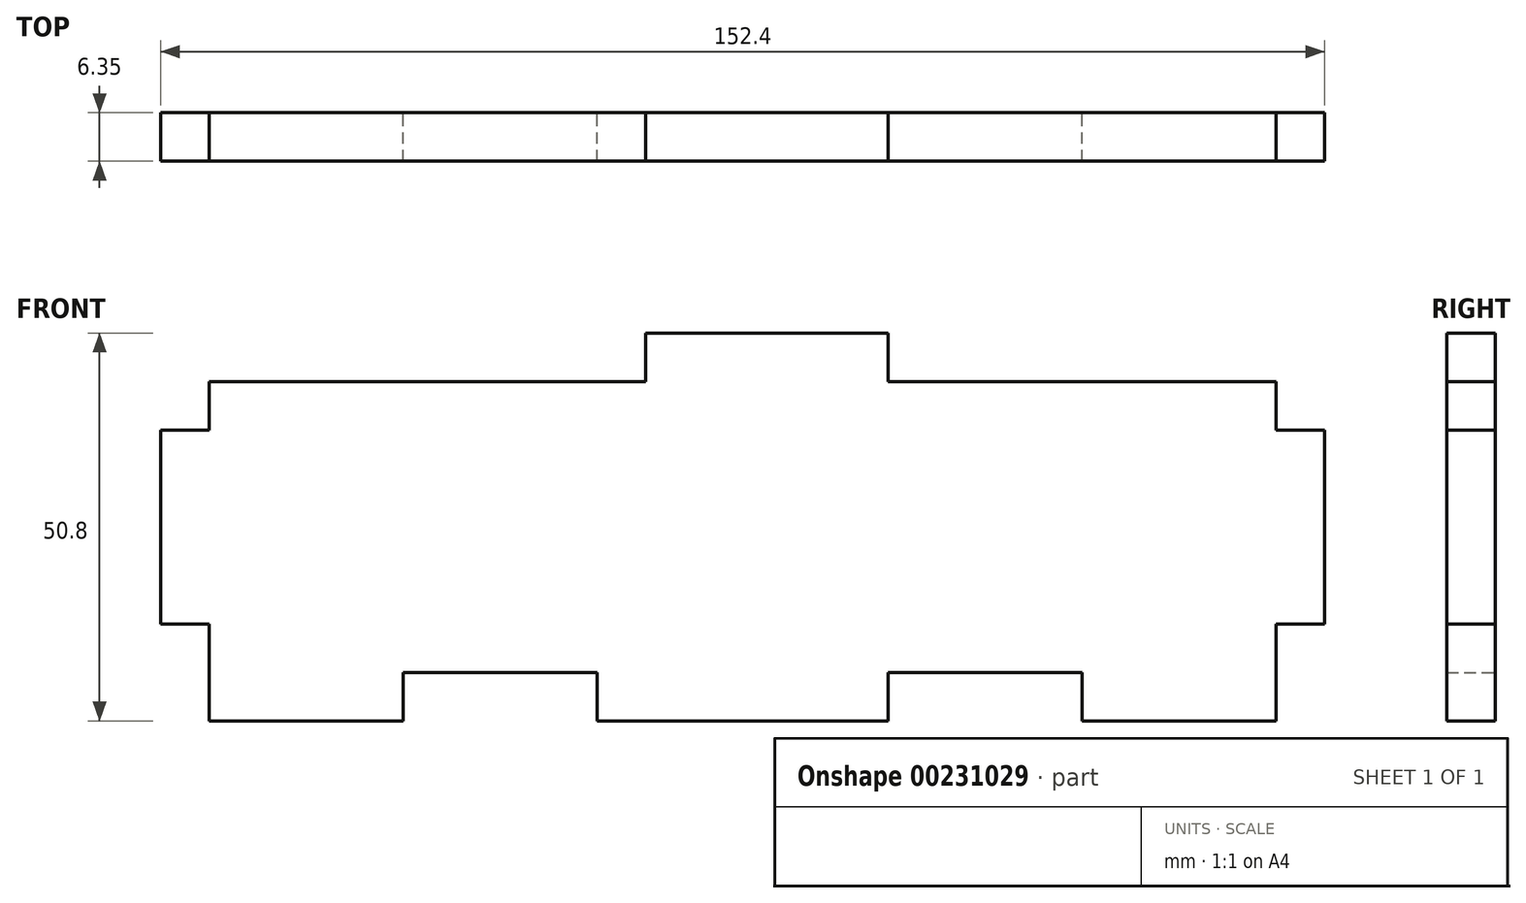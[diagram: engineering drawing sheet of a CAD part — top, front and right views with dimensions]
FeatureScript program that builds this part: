
annotation { "Feature Type Name" : "Feature", "Feature Type Description" : "" }
export const myFeature = defineFeature(function(context is Context, id is Id, definition is map)
    precondition{}
    {
        {
            var Q0;
            Q0=qCreatedBy(makeId("Front.planeOp"),FACE);
            var sketch = newSketch(context, id + "F0", { "sketchPlane" : qUnion([Q0])});
            skLineSegment(sketch, "E0.left", {"start": v(-76.2, 12.7) * mm, "end": v(-76.2, 6.35) * mm});
            skPoint(sketch, "E0.middle", {"position": v(0, 0) * mm});
            skLineSegment(sketch, "E1.MirrorCS", {"start": v(19.05, 25.4) * mm, "end": v(19.05, 19.05) * mm});
            skLineSegment(sketch, "E2.MirrorCS", {"start": v(-12.7, 25.4) * mm, "end": v(-12.7, 19.05) * mm});
            skLineSegment(sketch, "E3.MirrorCS", {"start": v(69.85, -25.4) * mm, "end": v(69.85, -19.05) * mm});
            skLineSegment(sketch, "E4.MirrorCS", {"start": v(44.45, -25.4) * mm, "end": v(44.45, -19.05) * mm});
            skLineSegment(sketch, "E5.MirrorCS", {"start": v(19.05, -25.4) * mm, "end": v(19.05, -19.05) * mm});
            skLineSegment(sketch, "E6.MirrorCS", {"start": v(-44.45, -25.4) * mm, "end": v(-44.45, -19.05) * mm});
            skLineSegment(sketch, "E7.MirrorCS", {"start": v(76.2, -12.7) * mm, "end": v(69.85, -12.7) * mm});
            skLineSegment(sketch, "E8.MirrorCS", {"start": v(-69.85, 19.05) * mm, "end": v(-69.85, 12.7) * mm});
            skLineSegment(sketch, "E9.MirrorCS", {"start": v(-76.2, 12.7) * mm, "end": v(-69.85, 12.7) * mm});
            skPoint(sketch, "E10.orphan", {"position": v(69.85, -127) * mm});
            skPoint(sketch, "E11.orphan", {"position": v(-69.85, -127) * mm});
            skLineSegment(sketch, "E12.trimOffspring", {"start": v(12.7, 25.4) * mm, "end": v(19.05, 25.4) * mm});
            skLineSegment(sketch, "E13.trimOffspring", {"start": v(0, 25.4) * mm, "end": v(6.35, 25.4) * mm});
            skLineSegment(sketch, "E14.trimOffspring", {"start": v(-12.7, 25.4) * mm, "end": v(-6.35, 25.4) * mm});
            skPoint(sketch, "E15.MirrorCS.end.orphan", {"position": v(-69.85, 19.05) * mm});
            skLineSegment(sketch, "E16.trimOffspring", {"start": v(63.5, -25.4) * mm, "end": v(69.85, -25.4) * mm});
            skLineSegment(sketch, "E17.trimOffspring", {"start": v(50.8, -25.4) * mm, "end": v(57.15, -25.4) * mm});
            skLineSegment(sketch, "E18.trimOffspring", {"start": v(12.7, -25.4) * mm, "end": v(19.05, -25.4) * mm});
            skLineSegment(sketch, "E19.trimOffspring", {"start": v(0, -25.4) * mm, "end": v(6.35, -25.4) * mm});
            skLineSegment(sketch, "E20.trimOffspring", {"start": v(-12.7, -25.4) * mm, "end": v(-6.35, -25.4) * mm});
            skLineSegment(sketch, "E21.trimOffspring", {"start": v(-50.8, -25.4) * mm, "end": v(-44.45, -25.4) * mm});
            skLineSegment(sketch, "E22.trimOffspring", {"start": v(-63.5, -25.4) * mm, "end": v(-57.15, -25.4) * mm});
            skLineSegment(sketch, "E23.trimOffspring", {"start": v(-76.2, 0) * mm, "end": v(-76.2, -6.35) * mm});
            skLineSegment(sketch, "E24.trimOffspring", {"start": v(76.2, -6.35) * mm, "end": v(76.2, -12.7) * mm});
            skLineSegment(sketch, "E25.trimOffspring", {"start": v(76.2, 6.35) * mm, "end": v(76.2, 0) * mm});
            skLineSegment(sketch, "E26.trimOffspring", {"start": v(50.8, 19.05) * mm, "end": v(44.45, 19.05) * mm});
            skLineSegment(sketch, "E27.trimOffspring", {"start": v(38.1, 19.05) * mm, "end": v(31.75, 19.05) * mm});
            skLineSegment(sketch, "E28.trimOffspring", {"start": v(25.4, 19.05) * mm, "end": v(19.05, 19.05) * mm});
            skLineSegment(sketch, "E29.trimOffspring", {"start": v(-12.7, 19.05) * mm, "end": v(-19.05, 19.05) * mm});
            skLineSegment(sketch, "E30.trimOffspring", {"start": v(-25.4, 19.05) * mm, "end": v(-31.75, 19.05) * mm});
            skLineSegment(sketch, "E31.trimOffspring", {"start": v(-38.1, 19.05) * mm, "end": v(-44.45, 19.05) * mm});
            skLineSegment(sketch, "E32.trimOffspring", {"start": v(-50.8, 19.05) * mm, "end": v(-57.15, 19.05) * mm});
            skPoint(sketch, "E33.orphan", {"position": v(-69.85, -19.05) * mm});
            skLineSegment(sketch, "E34.trimOffspring", {"start": v(-38.1, -19.05) * mm, "end": v(-44.45, -19.05) * mm});
            skLineSegment(sketch, "E35.trimOffspring", {"start": v(-25.4, -19.05) * mm, "end": v(-31.75, -19.05) * mm});
            skLineSegment(sketch, "E36.trimOffspring", {"start": v(25.4, -19.05) * mm, "end": v(19.05, -19.05) * mm});
            skLineSegment(sketch, "E37.trimOffspring", {"start": v(38.1, -19.05) * mm, "end": v(31.75, -19.05) * mm});
            skLineSegment(sketch, "E38.trimOffspring", {"start": v(69.85, -12.7) * mm, "end": v(69.85, -25.4) * mm});
            skLineSegment(sketch, "E39", {"start": v(-69.85, -12.7) * mm, "end": v(-69.85, -19.05) * mm});
            skLineSegment(sketch, "E40.bottom", {"start": v(-63.5, -25.4) * mm, "end": v(-69.85, -25.4) * mm});
            skLineSegment(sketch, "E40.right", {"start": v(-69.85, -25.4) * mm, "end": v(-69.85, -19.05) * mm});
            skLineSegment(sketch, "E41", {"start": v(-76.2, 6.35) * mm, "end": v(-76.2, 0) * mm});
            skLineSegment(sketch, "E42.bottom", {"start": v(-69.85, -12.7) * mm, "end": v(-76.2, -12.7) * mm});
            skLineSegment(sketch, "E42.right", {"start": v(-76.2, -12.7) * mm, "end": v(-76.2, -6.35) * mm});
            skLineSegment(sketch, "E43", {"start": v(-57.15, -25.4) * mm, "end": v(-50.8, -25.4) * mm});
            skLineSegment(sketch, "E44", {"start": v(-38.1, -19.05) * mm, "end": v(-31.75, -19.05) * mm});
            skLineSegment(sketch, "E45", {"start": v(-25.4, -19.05) * mm, "end": v(-19.05, -19.05) * mm});
            skLineSegment(sketch, "E46.top", {"start": v(-19.05, -25.4) * mm, "end": v(-12.7, -25.4) * mm});
            skLineSegment(sketch, "E46.left", {"start": v(-19.05, -19.05) * mm, "end": v(-19.05, -25.4) * mm});
            skLineSegment(sketch, "E47", {"start": v(-6.35, -25.4) * mm, "end": v(0, -25.4) * mm});
            skLineSegment(sketch, "E48", {"start": v(57.15, -25.4) * mm, "end": v(63.5, -25.4) * mm});
            skLineSegment(sketch, "E49", {"start": v(44.45, -25.4) * mm, "end": v(50.8, -25.4) * mm});
            skLineSegment(sketch, "E50", {"start": v(44.45, -19.05) * mm, "end": v(38.1, -19.05) * mm});
            skLineSegment(sketch, "E51", {"start": v(25.4, -19.05) * mm, "end": v(31.75, -19.05) * mm});
            skLineSegment(sketch, "E52", {"start": v(6.35, -25.4) * mm, "end": v(12.7, -25.4) * mm});
            skLineSegment(sketch, "E53", {"start": v(69.85, 19.05) * mm, "end": v(69.85, 12.7) * mm});
            skLineSegment(sketch, "E54.bottom", {"start": v(69.85, 12.7) * mm, "end": v(76.2, 12.7) * mm});
            skLineSegment(sketch, "E54.right", {"start": v(76.2, 12.7) * mm, "end": v(76.2, 6.35) * mm});
            skLineSegment(sketch, "E55", {"start": v(76.2, 0) * mm, "end": v(76.2, -6.35) * mm});
            skLineSegment(sketch, "E56.top", {"start": v(63.5, 19.05) * mm, "end": v(57.15, 19.05) * mm});
            skLineSegment(sketch, "E57", {"start": v(12.7, 25.4) * mm, "end": v(6.35, 25.4) * mm});
            skLineSegment(sketch, "E58", {"start": v(0, 25.4) * mm, "end": v(-6.35, 25.4) * mm});
            skLineSegment(sketch, "E59", {"start": v(57.15, 19.05) * mm, "end": v(50.8, 19.05) * mm});
            skLineSegment(sketch, "E60", {"start": v(44.45, 19.05) * mm, "end": v(38.1, 19.05) * mm});
            skLineSegment(sketch, "E61", {"start": v(31.75, 19.05) * mm, "end": v(25.4, 19.05) * mm});
            skLineSegment(sketch, "E62", {"start": v(63.5, 19.05) * mm, "end": v(69.85, 19.05) * mm});
            skLineSegment(sketch, "E63", {"start": v(-19.05, 19.05) * mm, "end": v(-25.4, 19.05) * mm});
            skLineSegment(sketch, "E64", {"start": v(-31.75, 19.05) * mm, "end": v(-38.1, 19.05) * mm});
            skLineSegment(sketch, "E65", {"start": v(-44.45, 19.05) * mm, "end": v(-50.8, 19.05) * mm});
            skLineSegment(sketch, "E66", {"start": v(-57.15, 19.05) * mm, "end": v(-69.85, 19.05) * mm});
            skSolve(sketch);
        }
        {
            var Q0;
            Q0 = qSketchRegion(id + "F0", true);
            extrude(context, id + "F1", {"entities" : qUnion([Q0]), "depth" : 6.35 * mm});
        }
    });
